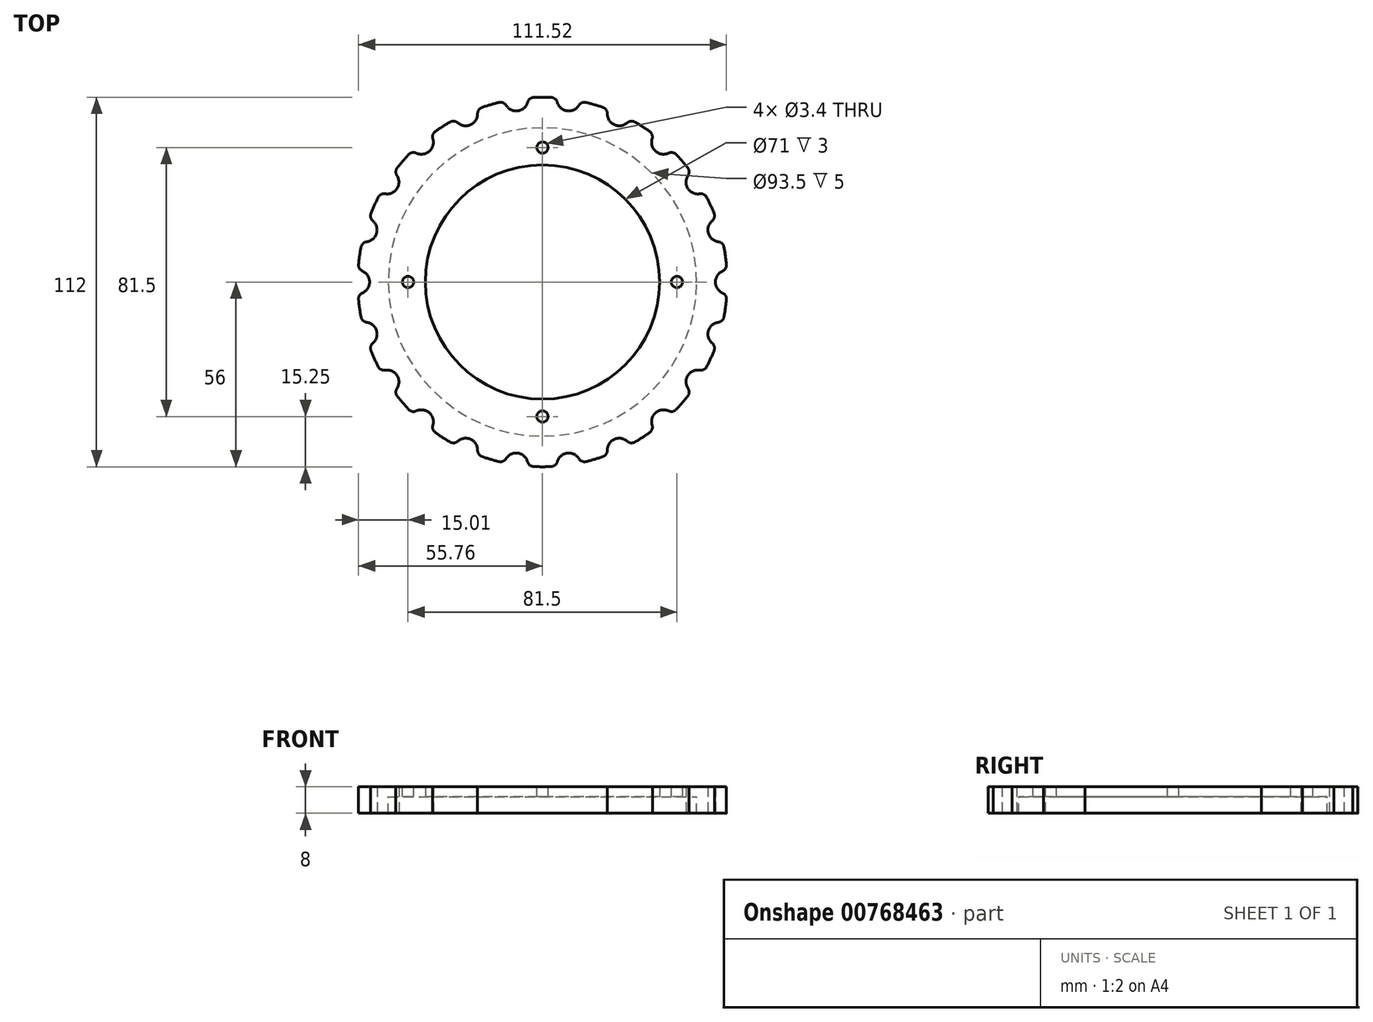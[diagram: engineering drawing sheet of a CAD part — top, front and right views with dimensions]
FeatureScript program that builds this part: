
annotation { "Feature Type Name" : "Feature", "Feature Type Description" : "" }
export const myFeature = defineFeature(function(context is Context, id is Id, definition is map)
    precondition{}
    {
        {
            var Q0;
            Q0=qCreatedBy(makeId("Top.planeOp"),FACE);
            var sketch = newSketch(context, id + "F0", { "sketchPlane" : qUnion([Q0])});
            skCircle(sketch, "E0", {"center": v(0, 0) * mm, "radius": 56 * mm});
            skCircle(sketch, "E1", {"center": v(56, 0) * mm, "radius": 3.6 * mm});
            skCircle(sketch, "E2.1.0", {"center": v(53.73, 15.78) * mm, "radius": 3.6 * mm});
            skCircle(sketch, "E2.2.0", {"center": v(47.11, 30.28) * mm, "radius": 3.6 * mm});
            skCircle(sketch, "E2.3.0", {"center": v(36.67, 42.32) * mm, "radius": 3.6 * mm});
            skCircle(sketch, "E2.4.0", {"center": v(23.26, 50.94) * mm, "radius": 3.6 * mm});
            skCircle(sketch, "E2.5.0", {"center": v(7.97, 55.43) * mm, "radius": 3.6 * mm});
            skCircle(sketch, "E2.6.0", {"center": v(-7.97, 55.43) * mm, "radius": 3.6 * mm});
            skCircle(sketch, "E2.7.0", {"center": v(-23.26, 50.94) * mm, "radius": 3.6 * mm});
            skCircle(sketch, "E2.8.0", {"center": v(-36.67, 42.32) * mm, "radius": 3.6 * mm});
            skCircle(sketch, "E2.9.0", {"center": v(-47.11, 30.28) * mm, "radius": 3.6 * mm});
            skCircle(sketch, "E2.10.0", {"center": v(-53.73, 15.78) * mm, "radius": 3.6 * mm});
            skCircle(sketch, "E2.11.0", {"center": v(-56, 0) * mm, "radius": 3.6 * mm});
            skCircle(sketch, "E2.12.0", {"center": v(-53.73, -15.78) * mm, "radius": 3.6 * mm});
            skCircle(sketch, "E2.13.0", {"center": v(-47.11, -30.28) * mm, "radius": 3.6 * mm});
            skCircle(sketch, "E2.14.0", {"center": v(-36.67, -42.32) * mm, "radius": 3.6 * mm});
            skCircle(sketch, "E2.15.0", {"center": v(-23.26, -50.94) * mm, "radius": 3.6 * mm});
            skCircle(sketch, "E2.16.0", {"center": v(-7.97, -55.43) * mm, "radius": 3.6 * mm});
            skCircle(sketch, "E2.17.0", {"center": v(7.97, -55.43) * mm, "radius": 3.6 * mm});
            skCircle(sketch, "E3.1.18.0", {"center": v(23.26, -50.94) * mm, "radius": 3.6 * mm});
            skCircle(sketch, "E4.1.19.0", {"center": v(36.67, -42.32) * mm, "radius": 3.6 * mm});
            skCircle(sketch, "E5.1.20.0", {"center": v(47.11, -30.28) * mm, "radius": 3.6 * mm});
            skCircle(sketch, "E6.1.21.0", {"center": v(53.73, -15.78) * mm, "radius": 3.6 * mm});
            skCircle(sketch, "E7", {"center": v(0, 0) * mm, "radius": 35.5 * mm});
            skSolve(sketch);
        }
        {
            var Q0;
            Q0=makeQuery(id+"F0.imprint","IMPRINT",FACE,{"disambiguationData":[TD([[makeQuery(id+"F0.imprint","IMPRINT",EDGE,{"derivedFrom":sQuery(id+"F0.wireOp",EDGE,"E0")}),1.0]])]});
            extrude(context, id + "F1", {"entities" : qUnion([Q0]), "depth" : 3 * mm, "offsetDistance" : 25 * mm});
        }
        {
            var Q0;
            {var subQ0=sQuery(id+"F0.wireOp",EDGE,"E2.7.0");var subQ1=sQuery(id+"F0.wireOp",EDGE,"E0");Q0=makeQuery(id+"F1.opExtrude","SWEPT_EDGE",EDGE,{"disambiguationData":[OSD([subQ1,subQ0]),TDD([makeQuery(id+"F0.imprint","INTERSECT",VERTEX,{"disambiguationData":[OD(1.0)],"derivedFrom":[subQ1,subQ0]})])]});}
            var Q1;
            {var subQ0=sQuery(id+"F0.wireOp",EDGE,"E2.8.0");var subQ1=sQuery(id+"F0.wireOp",EDGE,"E0");Q1=makeQuery(id+"F1.opExtrude","SWEPT_EDGE",EDGE,{"disambiguationData":[OSD([subQ1,subQ0]),TDD([makeQuery(id+"F0.imprint","INTERSECT",VERTEX,{"disambiguationData":[OD(0.0)],"derivedFrom":[subQ1,subQ0]})])]});}
            var Q2;
            {var subQ0=sQuery(id+"F0.wireOp",EDGE,"E2.8.0");var subQ1=sQuery(id+"F0.wireOp",EDGE,"E0");Q2=makeQuery(id+"F1.opExtrude","SWEPT_EDGE",EDGE,{"disambiguationData":[OSD([subQ1,subQ0]),TDD([makeQuery(id+"F0.imprint","INTERSECT",VERTEX,{"disambiguationData":[OD(1.0)],"derivedFrom":[subQ1,subQ0]})])]});}
            var Q3;
            {var subQ0=sQuery(id+"F0.wireOp",EDGE,"E2.9.0");var subQ1=sQuery(id+"F0.wireOp",EDGE,"E0");Q3=makeQuery(id+"F1.opExtrude","SWEPT_EDGE",EDGE,{"disambiguationData":[OSD([subQ1,subQ0]),TDD([makeQuery(id+"F0.imprint","INTERSECT",VERTEX,{"disambiguationData":[OD(0.0)],"derivedFrom":[subQ1,subQ0]})])]});}
            var Q4;
            {var subQ0=sQuery(id+"F0.wireOp",EDGE,"E2.9.0");var subQ1=sQuery(id+"F0.wireOp",EDGE,"E0");Q4=makeQuery(id+"F1.opExtrude","SWEPT_EDGE",EDGE,{"disambiguationData":[OSD([subQ1,subQ0]),TDD([makeQuery(id+"F0.imprint","INTERSECT",VERTEX,{"disambiguationData":[OD(1.0)],"derivedFrom":[subQ1,subQ0]})])]});}
            var Q5;
            {var subQ0=sQuery(id+"F0.wireOp",EDGE,"E2.10.0");var subQ1=sQuery(id+"F0.wireOp",EDGE,"E0");Q5=makeQuery(id+"F1.opExtrude","SWEPT_EDGE",EDGE,{"disambiguationData":[OSD([subQ1,subQ0]),TDD([makeQuery(id+"F0.imprint","INTERSECT",VERTEX,{"disambiguationData":[OD(0.0)],"derivedFrom":[subQ1,subQ0]})])]});}
            var Q6;
            {var subQ0=sQuery(id+"F0.wireOp",EDGE,"E2.10.0");var subQ1=sQuery(id+"F0.wireOp",EDGE,"E0");Q6=makeQuery(id+"F1.opExtrude","SWEPT_EDGE",EDGE,{"disambiguationData":[OSD([subQ1,subQ0]),TDD([makeQuery(id+"F0.imprint","INTERSECT",VERTEX,{"disambiguationData":[OD(1.0)],"derivedFrom":[subQ1,subQ0]})])]});}
            var Q7;
            {var subQ0=sQuery(id+"F0.wireOp",EDGE,"E2.11.0");var subQ1=sQuery(id+"F0.wireOp",EDGE,"E0");Q7=makeQuery(id+"F1.opExtrude","SWEPT_EDGE",EDGE,{"disambiguationData":[OSD([subQ1,subQ0]),TDD([makeQuery(id+"F0.imprint","INTERSECT",VERTEX,{"disambiguationData":[OD(0.0)],"derivedFrom":[subQ1,subQ0]})])]});}
            var Q8;
            {var subQ0=sQuery(id+"F0.wireOp",EDGE,"E2.11.0");var subQ1=sQuery(id+"F0.wireOp",EDGE,"E0");Q8=makeQuery(id+"F1.opExtrude","SWEPT_EDGE",EDGE,{"disambiguationData":[OSD([subQ1,subQ0]),TDD([makeQuery(id+"F0.imprint","INTERSECT",VERTEX,{"disambiguationData":[OD(1.0)],"derivedFrom":[subQ1,subQ0]})])]});}
            var Q9;
            {var subQ0=sQuery(id+"F0.wireOp",EDGE,"E2.12.0");var subQ1=sQuery(id+"F0.wireOp",EDGE,"E0");Q9=makeQuery(id+"F1.opExtrude","SWEPT_EDGE",EDGE,{"disambiguationData":[OSD([subQ1,subQ0]),TDD([makeQuery(id+"F0.imprint","INTERSECT",VERTEX,{"disambiguationData":[OD(0.0)],"derivedFrom":[subQ1,subQ0]})])]});}
            var Q10;
            {var subQ0=sQuery(id+"F0.wireOp",EDGE,"E2.12.0");var subQ1=sQuery(id+"F0.wireOp",EDGE,"E0");Q10=makeQuery(id+"F1.opExtrude","SWEPT_EDGE",EDGE,{"disambiguationData":[OSD([subQ1,subQ0]),TDD([makeQuery(id+"F0.imprint","INTERSECT",VERTEX,{"disambiguationData":[OD(1.0)],"derivedFrom":[subQ1,subQ0]})])]});}
            var Q11;
            {var subQ0=sQuery(id+"F0.wireOp",EDGE,"E2.13.0");var subQ1=sQuery(id+"F0.wireOp",EDGE,"E0");Q11=makeQuery(id+"F1.opExtrude","SWEPT_EDGE",EDGE,{"disambiguationData":[OSD([subQ1,subQ0]),TDD([makeQuery(id+"F0.imprint","INTERSECT",VERTEX,{"disambiguationData":[OD(0.0)],"derivedFrom":[subQ1,subQ0]})])]});}
            var Q12;
            {var subQ0=sQuery(id+"F0.wireOp",EDGE,"E2.13.0");var subQ1=sQuery(id+"F0.wireOp",EDGE,"E0");Q12=makeQuery(id+"F1.opExtrude","SWEPT_EDGE",EDGE,{"disambiguationData":[OSD([subQ1,subQ0]),TDD([makeQuery(id+"F0.imprint","INTERSECT",VERTEX,{"disambiguationData":[OD(1.0)],"derivedFrom":[subQ1,subQ0]})])]});}
            var Q13;
            {var subQ0=sQuery(id+"F0.wireOp",EDGE,"E2.14.0");var subQ1=sQuery(id+"F0.wireOp",EDGE,"E0");Q13=makeQuery(id+"F1.opExtrude","SWEPT_EDGE",EDGE,{"disambiguationData":[OSD([subQ1,subQ0]),TDD([makeQuery(id+"F0.imprint","INTERSECT",VERTEX,{"disambiguationData":[OD(0.0)],"derivedFrom":[subQ1,subQ0]})])]});}
            var Q14;
            {var subQ0=sQuery(id+"F0.wireOp",EDGE,"E2.14.0");var subQ1=sQuery(id+"F0.wireOp",EDGE,"E0");Q14=makeQuery(id+"F1.opExtrude","SWEPT_EDGE",EDGE,{"disambiguationData":[OSD([subQ1,subQ0]),TDD([makeQuery(id+"F0.imprint","INTERSECT",VERTEX,{"disambiguationData":[OD(1.0)],"derivedFrom":[subQ1,subQ0]})])]});}
            var Q15;
            {var subQ0=sQuery(id+"F0.wireOp",EDGE,"E2.15.0");var subQ1=sQuery(id+"F0.wireOp",EDGE,"E0");Q15=makeQuery(id+"F1.opExtrude","SWEPT_EDGE",EDGE,{"disambiguationData":[OSD([subQ1,subQ0]),TDD([makeQuery(id+"F0.imprint","INTERSECT",VERTEX,{"disambiguationData":[OD(0.0)],"derivedFrom":[subQ1,subQ0]})])]});}
            var Q16;
            {var subQ0=sQuery(id+"F0.wireOp",EDGE,"E2.15.0");var subQ1=sQuery(id+"F0.wireOp",EDGE,"E0");Q16=makeQuery(id+"F1.opExtrude","SWEPT_EDGE",EDGE,{"disambiguationData":[OSD([subQ1,subQ0]),TDD([makeQuery(id+"F0.imprint","INTERSECT",VERTEX,{"disambiguationData":[OD(1.0)],"derivedFrom":[subQ1,subQ0]})])]});}
            var Q17;
            {var subQ0=sQuery(id+"F0.wireOp",EDGE,"E2.16.0");var subQ1=sQuery(id+"F0.wireOp",EDGE,"E0");Q17=makeQuery(id+"F1.opExtrude","SWEPT_EDGE",EDGE,{"disambiguationData":[OSD([subQ1,subQ0]),TDD([makeQuery(id+"F0.imprint","INTERSECT",VERTEX,{"disambiguationData":[OD(0.0)],"derivedFrom":[subQ1,subQ0]})])]});}
            var Q18;
            {var subQ0=sQuery(id+"F0.wireOp",EDGE,"E2.16.0");var subQ1=sQuery(id+"F0.wireOp",EDGE,"E0");Q18=makeQuery(id+"F1.opExtrude","SWEPT_EDGE",EDGE,{"disambiguationData":[OSD([subQ1,subQ0]),TDD([makeQuery(id+"F0.imprint","INTERSECT",VERTEX,{"disambiguationData":[OD(1.0)],"derivedFrom":[subQ1,subQ0]})])]});}
            var Q19;
            {var subQ0=sQuery(id+"F0.wireOp",EDGE,"E2.17.0");var subQ1=sQuery(id+"F0.wireOp",EDGE,"E0");Q19=makeQuery(id+"F1.opExtrude","SWEPT_EDGE",EDGE,{"disambiguationData":[OSD([subQ1,subQ0]),TDD([makeQuery(id+"F0.imprint","INTERSECT",VERTEX,{"disambiguationData":[OD(0.0)],"derivedFrom":[subQ1,subQ0]})])]});}
            var Q20;
            {var subQ0=sQuery(id+"F0.wireOp",EDGE,"E2.17.0");var subQ1=sQuery(id+"F0.wireOp",EDGE,"E0");Q20=makeQuery(id+"F1.opExtrude","SWEPT_EDGE",EDGE,{"disambiguationData":[OSD([subQ1,subQ0]),TDD([makeQuery(id+"F0.imprint","INTERSECT",VERTEX,{"disambiguationData":[OD(1.0)],"derivedFrom":[subQ1,subQ0]})])]});}
            var Q21;
            {var subQ0=sQuery(id+"F0.wireOp",EDGE,"E3.1.18.0");var subQ1=sQuery(id+"F0.wireOp",EDGE,"E0");Q21=makeQuery(id+"F1.opExtrude","SWEPT_EDGE",EDGE,{"disambiguationData":[OSD([subQ1,subQ0]),TDD([makeQuery(id+"F0.imprint","INTERSECT",VERTEX,{"disambiguationData":[OD(0.0)],"derivedFrom":[subQ1,subQ0]})])]});}
            var Q22;
            {var subQ0=sQuery(id+"F0.wireOp",EDGE,"E4.1.19.0");var subQ1=sQuery(id+"F0.wireOp",EDGE,"E0");Q22=makeQuery(id+"F1.opExtrude","SWEPT_EDGE",EDGE,{"disambiguationData":[OSD([subQ1,subQ0]),TDD([makeQuery(id+"F0.imprint","INTERSECT",VERTEX,{"disambiguationData":[OD(0.0)],"derivedFrom":[subQ1,subQ0]})])]});}
            var Q23;
            {var subQ0=sQuery(id+"F0.wireOp",EDGE,"E3.1.18.0");var subQ1=sQuery(id+"F0.wireOp",EDGE,"E0");Q23=makeQuery(id+"F1.opExtrude","SWEPT_EDGE",EDGE,{"disambiguationData":[OSD([subQ1,subQ0]),TDD([makeQuery(id+"F0.imprint","INTERSECT",VERTEX,{"disambiguationData":[OD(1.0)],"derivedFrom":[subQ1,subQ0]})])]});}
            var Q24;
            {var subQ0=sQuery(id+"F0.wireOp",EDGE,"E4.1.19.0");var subQ1=sQuery(id+"F0.wireOp",EDGE,"E0");Q24=makeQuery(id+"F1.opExtrude","SWEPT_EDGE",EDGE,{"disambiguationData":[OSD([subQ1,subQ0]),TDD([makeQuery(id+"F0.imprint","INTERSECT",VERTEX,{"disambiguationData":[OD(1.0)],"derivedFrom":[subQ1,subQ0]})])]});}
            var Q25;
            {var subQ0=sQuery(id+"F0.wireOp",EDGE,"E5.1.20.0");var subQ1=sQuery(id+"F0.wireOp",EDGE,"E0");Q25=makeQuery(id+"F1.opExtrude","SWEPT_EDGE",EDGE,{"disambiguationData":[OSD([subQ1,subQ0]),TDD([makeQuery(id+"F0.imprint","INTERSECT",VERTEX,{"disambiguationData":[OD(0.0)],"derivedFrom":[subQ1,subQ0]})])]});}
            var Q26;
            {var subQ0=sQuery(id+"F0.wireOp",EDGE,"E6.1.21.0");var subQ1=sQuery(id+"F0.wireOp",EDGE,"E0");Q26=makeQuery(id+"F1.opExtrude","SWEPT_EDGE",EDGE,{"disambiguationData":[OSD([subQ1,subQ0]),TDD([makeQuery(id+"F0.imprint","INTERSECT",VERTEX,{"disambiguationData":[OD(0.0)],"derivedFrom":[subQ1,subQ0]})])]});}
            var Q27;
            {var subQ0=sQuery(id+"F0.wireOp",EDGE,"E5.1.20.0");var subQ1=sQuery(id+"F0.wireOp",EDGE,"E0");Q27=makeQuery(id+"F1.opExtrude","SWEPT_EDGE",EDGE,{"disambiguationData":[OSD([subQ1,subQ0]),TDD([makeQuery(id+"F0.imprint","INTERSECT",VERTEX,{"disambiguationData":[OD(1.0)],"derivedFrom":[subQ1,subQ0]})])]});}
            var Q28;
            {var subQ0=sQuery(id+"F0.wireOp",EDGE,"E1");var subQ1=sQuery(id+"F0.wireOp",EDGE,"E0");Q28=makeQuery(id+"F1.opExtrude","SWEPT_EDGE",EDGE,{"disambiguationData":[OSD([subQ1,subQ0]),TDD([makeQuery(id+"F0.imprint","INTERSECT",VERTEX,{"disambiguationData":[OD(1.0)],"derivedFrom":[subQ1,subQ0]})])]});}
            var Q29;
            {var subQ0=sQuery(id+"F0.wireOp",EDGE,"E6.1.21.0");var subQ1=sQuery(id+"F0.wireOp",EDGE,"E0");Q29=makeQuery(id+"F1.opExtrude","SWEPT_EDGE",EDGE,{"disambiguationData":[OSD([subQ1,subQ0]),TDD([makeQuery(id+"F0.imprint","INTERSECT",VERTEX,{"disambiguationData":[OD(1.0)],"derivedFrom":[subQ1,subQ0]})])]});}
            var Q30;
            {var subQ0=sQuery(id+"F0.wireOp",EDGE,"E1");var subQ1=sQuery(id+"F0.wireOp",EDGE,"E0");Q30=makeQuery(id+"F1.opExtrude","SWEPT_EDGE",EDGE,{"disambiguationData":[OSD([subQ1,subQ0]),TDD([makeQuery(id+"F0.imprint","INTERSECT",VERTEX,{"disambiguationData":[OD(0.0)],"derivedFrom":[subQ1,subQ0]})])]});}
            var Q31;
            {var subQ0=sQuery(id+"F0.wireOp",EDGE,"E2.1.0");var subQ1=sQuery(id+"F0.wireOp",EDGE,"E0");Q31=makeQuery(id+"F1.opExtrude","SWEPT_EDGE",EDGE,{"disambiguationData":[OSD([subQ1,subQ0]),TDD([makeQuery(id+"F0.imprint","INTERSECT",VERTEX,{"disambiguationData":[OD(0.0)],"derivedFrom":[subQ1,subQ0]})])]});}
            var Q32;
            {var subQ0=sQuery(id+"F0.wireOp",EDGE,"E2.1.0");var subQ1=sQuery(id+"F0.wireOp",EDGE,"E0");Q32=makeQuery(id+"F1.opExtrude","SWEPT_EDGE",EDGE,{"disambiguationData":[OSD([subQ1,subQ0]),TDD([makeQuery(id+"F0.imprint","INTERSECT",VERTEX,{"disambiguationData":[OD(1.0)],"derivedFrom":[subQ1,subQ0]})])]});}
            var Q33;
            {var subQ0=sQuery(id+"F0.wireOp",EDGE,"E2.2.0");var subQ1=sQuery(id+"F0.wireOp",EDGE,"E0");Q33=makeQuery(id+"F1.opExtrude","SWEPT_EDGE",EDGE,{"disambiguationData":[OSD([subQ1,subQ0]),TDD([makeQuery(id+"F0.imprint","INTERSECT",VERTEX,{"disambiguationData":[OD(0.0)],"derivedFrom":[subQ1,subQ0]})])]});}
            var Q34;
            {var subQ0=sQuery(id+"F0.wireOp",EDGE,"E2.2.0");var subQ1=sQuery(id+"F0.wireOp",EDGE,"E0");Q34=makeQuery(id+"F1.opExtrude","SWEPT_EDGE",EDGE,{"disambiguationData":[OSD([subQ1,subQ0]),TDD([makeQuery(id+"F0.imprint","INTERSECT",VERTEX,{"disambiguationData":[OD(1.0)],"derivedFrom":[subQ1,subQ0]})])]});}
            var Q35;
            {var subQ0=sQuery(id+"F0.wireOp",EDGE,"E2.3.0");var subQ1=sQuery(id+"F0.wireOp",EDGE,"E0");Q35=makeQuery(id+"F1.opExtrude","SWEPT_EDGE",EDGE,{"disambiguationData":[OSD([subQ1,subQ0]),TDD([makeQuery(id+"F0.imprint","INTERSECT",VERTEX,{"disambiguationData":[OD(0.0)],"derivedFrom":[subQ1,subQ0]})])]});}
            var Q36;
            {var subQ0=sQuery(id+"F0.wireOp",EDGE,"E2.3.0");var subQ1=sQuery(id+"F0.wireOp",EDGE,"E0");Q36=makeQuery(id+"F1.opExtrude","SWEPT_EDGE",EDGE,{"disambiguationData":[OSD([subQ1,subQ0]),TDD([makeQuery(id+"F0.imprint","INTERSECT",VERTEX,{"disambiguationData":[OD(1.0)],"derivedFrom":[subQ1,subQ0]})])]});}
            var Q37;
            {var subQ0=sQuery(id+"F0.wireOp",EDGE,"E2.4.0");var subQ1=sQuery(id+"F0.wireOp",EDGE,"E0");Q37=makeQuery(id+"F1.opExtrude","SWEPT_EDGE",EDGE,{"disambiguationData":[OSD([subQ1,subQ0]),TDD([makeQuery(id+"F0.imprint","INTERSECT",VERTEX,{"disambiguationData":[OD(0.0)],"derivedFrom":[subQ1,subQ0]})])]});}
            var Q38;
            {var subQ0=sQuery(id+"F0.wireOp",EDGE,"E2.4.0");var subQ1=sQuery(id+"F0.wireOp",EDGE,"E0");Q38=makeQuery(id+"F1.opExtrude","SWEPT_EDGE",EDGE,{"disambiguationData":[OSD([subQ1,subQ0]),TDD([makeQuery(id+"F0.imprint","INTERSECT",VERTEX,{"disambiguationData":[OD(1.0)],"derivedFrom":[subQ1,subQ0]})])]});}
            var Q39;
            {var subQ0=sQuery(id+"F0.wireOp",EDGE,"E2.5.0");var subQ1=sQuery(id+"F0.wireOp",EDGE,"E0");Q39=makeQuery(id+"F1.opExtrude","SWEPT_EDGE",EDGE,{"disambiguationData":[OSD([subQ1,subQ0]),TDD([makeQuery(id+"F0.imprint","INTERSECT",VERTEX,{"disambiguationData":[OD(0.0)],"derivedFrom":[subQ1,subQ0]})])]});}
            var Q40;
            {var subQ0=sQuery(id+"F0.wireOp",EDGE,"E2.5.0");var subQ1=sQuery(id+"F0.wireOp",EDGE,"E0");Q40=makeQuery(id+"F1.opExtrude","SWEPT_EDGE",EDGE,{"disambiguationData":[OSD([subQ1,subQ0]),TDD([makeQuery(id+"F0.imprint","INTERSECT",VERTEX,{"disambiguationData":[OD(1.0)],"derivedFrom":[subQ1,subQ0]})])]});}
            var Q41;
            {var subQ0=sQuery(id+"F0.wireOp",EDGE,"E2.6.0");var subQ1=sQuery(id+"F0.wireOp",EDGE,"E0");Q41=makeQuery(id+"F1.opExtrude","SWEPT_EDGE",EDGE,{"disambiguationData":[OSD([subQ1,subQ0]),TDD([makeQuery(id+"F0.imprint","INTERSECT",VERTEX,{"disambiguationData":[OD(0.0)],"derivedFrom":[subQ1,subQ0]})])]});}
            var Q42;
            {var subQ0=sQuery(id+"F0.wireOp",EDGE,"E2.7.0");var subQ1=sQuery(id+"F0.wireOp",EDGE,"E0");Q42=makeQuery(id+"F1.opExtrude","SWEPT_EDGE",EDGE,{"disambiguationData":[OSD([subQ1,subQ0]),TDD([makeQuery(id+"F0.imprint","INTERSECT",VERTEX,{"disambiguationData":[OD(0.0)],"derivedFrom":[subQ1,subQ0]})])]});}
            var Q43;
            {var subQ0=sQuery(id+"F0.wireOp",EDGE,"E2.6.0");var subQ1=sQuery(id+"F0.wireOp",EDGE,"E0");Q43=makeQuery(id+"F1.opExtrude","SWEPT_EDGE",EDGE,{"disambiguationData":[OSD([subQ1,subQ0]),TDD([makeQuery(id+"F0.imprint","INTERSECT",VERTEX,{"disambiguationData":[OD(1.0)],"derivedFrom":[subQ1,subQ0]})])]});}
            fillet(context, id + "F2", {"entities" : qUnion([Q0, Q1, Q2, Q3, Q4, Q5, Q6, Q7, Q8, Q9, Q10, Q11, Q12, Q13, Q14, Q15, Q16, Q17, Q18, Q19, Q20, Q21, Q22, Q23, Q24, Q25, Q26, Q27, Q28, Q29, Q30, Q31, Q32, Q33, Q34, Q35, Q36, Q37, Q38, Q39, Q40, Q41, Q42, Q43]), "tangentPropagation" : true, "radius" : 2 * mm, "defaultsChanged" : false, "vertexSettings" : [], "allowEdgeOverflow" : false});
        }
        {
            var Q0;
            Q0=makeQuery(id+"F1.opExtrude","CAP_FACE",FACE,{"disambiguationData":[OSD([sQuery(id+"F0.wireOp",EDGE,"E0"),sQuery(id+"F0.wireOp",EDGE,"E1"),sQuery(id+"F0.wireOp",EDGE,"E2.1.0"),sQuery(id+"F0.wireOp",EDGE,"E2.2.0"),sQuery(id+"F0.wireOp",EDGE,"E2.3.0"),sQuery(id+"F0.wireOp",EDGE,"E2.4.0"),sQuery(id+"F0.wireOp",EDGE,"E2.5.0"),sQuery(id+"F0.wireOp",EDGE,"E2.6.0"),sQuery(id+"F0.wireOp",EDGE,"E2.7.0"),sQuery(id+"F0.wireOp",EDGE,"E2.8.0"),sQuery(id+"F0.wireOp",EDGE,"E2.9.0"),sQuery(id+"F0.wireOp",EDGE,"E2.10.0"),sQuery(id+"F0.wireOp",EDGE,"E2.11.0"),sQuery(id+"F0.wireOp",EDGE,"E2.12.0"),sQuery(id+"F0.wireOp",EDGE,"E2.13.0"),sQuery(id+"F0.wireOp",EDGE,"E2.14.0"),sQuery(id+"F0.wireOp",EDGE,"E2.15.0"),sQuery(id+"F0.wireOp",EDGE,"E2.16.0"),sQuery(id+"F0.wireOp",EDGE,"E2.17.0"),sQuery(id+"F0.wireOp",EDGE,"E3.1.18.0"),sQuery(id+"F0.wireOp",EDGE,"E4.1.19.0"),sQuery(id+"F0.wireOp",EDGE,"E5.1.20.0"),sQuery(id+"F0.wireOp",EDGE,"E6.1.21.0"),sQuery(id+"F0.wireOp",EDGE,"E7")])],"isStart":false});
            var sketch = newSketch(context, id + "F3", { "sketchPlane" : qUnion([Q0])});
            skLineSegment(sketch, "E8", {"start": v(-40.75, 0) * mm, "end": v(0, 40.75) * mm});
            skLineSegment(sketch, "E9", {"start": v(0, 40.75) * mm, "end": v(40.75, 0) * mm});
            skLineSegment(sketch, "E10", {"start": v(40.75, 0) * mm, "end": v(0, -40.75) * mm});
            skLineSegment(sketch, "E11", {"start": v(0, -40.75) * mm, "end": v(-40.75, 0) * mm});
            skSolve(sketch);
        }
        {
            var Q0;
            Q0=sQuery(id+"F3.wireOp",VERTEX,"E8.end");
            var Q1;
            Q1=sQuery(id+"F3.wireOp",VERTEX,"E9.end");
            var Q2;
            Q2=sQuery(id+"F3.wireOp",VERTEX,"E10.end");
            var Q3;
            Q3=sQuery(id+"F3.wireOp",VERTEX,"E8.start");
            var Q4;
            Q4=makeQuery(id+"F1.opExtrude","SWEPT_BODY",BODY,{"disambiguationData":[OSD([sQuery(id+"F0.wireOp",EDGE,"E0"),sQuery(id+"F0.wireOp",EDGE,"E1"),sQuery(id+"F0.wireOp",EDGE,"E2.1.0"),sQuery(id+"F0.wireOp",EDGE,"E2.2.0"),sQuery(id+"F0.wireOp",EDGE,"E2.3.0"),sQuery(id+"F0.wireOp",EDGE,"E2.4.0"),sQuery(id+"F0.wireOp",EDGE,"E2.5.0"),sQuery(id+"F0.wireOp",EDGE,"E2.6.0"),sQuery(id+"F0.wireOp",EDGE,"E2.7.0"),sQuery(id+"F0.wireOp",EDGE,"E2.8.0"),sQuery(id+"F0.wireOp",EDGE,"E2.9.0"),sQuery(id+"F0.wireOp",EDGE,"E2.10.0"),sQuery(id+"F0.wireOp",EDGE,"E2.11.0"),sQuery(id+"F0.wireOp",EDGE,"E2.12.0"),sQuery(id+"F0.wireOp",EDGE,"E2.13.0"),sQuery(id+"F0.wireOp",EDGE,"E2.14.0"),sQuery(id+"F0.wireOp",EDGE,"E2.15.0"),sQuery(id+"F0.wireOp",EDGE,"E2.16.0"),sQuery(id+"F0.wireOp",EDGE,"E2.17.0"),sQuery(id+"F0.wireOp",EDGE,"E3.1.18.0"),sQuery(id+"F0.wireOp",EDGE,"E4.1.19.0"),sQuery(id+"F0.wireOp",EDGE,"E5.1.20.0"),sQuery(id+"F0.wireOp",EDGE,"E6.1.21.0"),sQuery(id+"F0.wireOp",EDGE,"E7")])]});
            hole(context, id + "F4", {"style" : HoleStyle.SIMPLE, "endStyle" : HoleEndStyle.THROUGH, "standardTappedOrClearance" : lookupTablePath({ "fit" : "Normal", "standard" : "ISO", "size" : "M3", "type" : "Clearance" }), "standardBlindInLast" : lookupTablePath({ "fit" : "Normal", "standard" : "ISO", "engagement" : "75%", "pitch" : "0.5 mm", "size" : "M3", "type" : "Clearance & tapped" }), "holeDiameter" : 3.4 * mm, "majorDiameter" : 5 * mm, "isTappedThrough" : true, "tappedDepth" : 12 * mm, "tapClearance" : 3, "locations" : qUnion([Q0, Q1, Q2, Q3]), "scope" : qUnion([Q4])});
        }
        {
            var Q0;
            Q0=makeQuery(id+"F1.opExtrude","CAP_FACE",FACE,{"disambiguationData":[OSD([sQuery(id+"F0.wireOp",EDGE,"E0"),sQuery(id+"F0.wireOp",EDGE,"E1"),sQuery(id+"F0.wireOp",EDGE,"E2.1.0"),sQuery(id+"F0.wireOp",EDGE,"E2.2.0"),sQuery(id+"F0.wireOp",EDGE,"E2.3.0"),sQuery(id+"F0.wireOp",EDGE,"E2.4.0"),sQuery(id+"F0.wireOp",EDGE,"E2.5.0"),sQuery(id+"F0.wireOp",EDGE,"E2.6.0"),sQuery(id+"F0.wireOp",EDGE,"E2.7.0"),sQuery(id+"F0.wireOp",EDGE,"E2.8.0"),sQuery(id+"F0.wireOp",EDGE,"E2.9.0"),sQuery(id+"F0.wireOp",EDGE,"E2.10.0"),sQuery(id+"F0.wireOp",EDGE,"E2.11.0"),sQuery(id+"F0.wireOp",EDGE,"E2.12.0"),sQuery(id+"F0.wireOp",EDGE,"E2.13.0"),sQuery(id+"F0.wireOp",EDGE,"E2.14.0"),sQuery(id+"F0.wireOp",EDGE,"E2.15.0"),sQuery(id+"F0.wireOp",EDGE,"E2.16.0"),sQuery(id+"F0.wireOp",EDGE,"E2.17.0"),sQuery(id+"F0.wireOp",EDGE,"E3.1.18.0"),sQuery(id+"F0.wireOp",EDGE,"E4.1.19.0"),sQuery(id+"F0.wireOp",EDGE,"E5.1.20.0"),sQuery(id+"F0.wireOp",EDGE,"E6.1.21.0"),sQuery(id+"F0.wireOp",EDGE,"E7")])],"isStart":true});
            var sketch = newSketch(context, id + "F5", { "sketchPlane" : qUnion([Q0])});
            skCircle(sketch, "E12", {"center": v(0, 0) * mm, "radius": 46.75 * mm});
            skSolve(sketch);
        }
        {
            var Q0;
            Q0=makeQuery(id+"F5.imprint","IMPRINT",FACE,{"disambiguationData":[TD([[makeQuery(id+"F5.imprint","IMPRINT",EDGE,{"derivedFrom":sQuery(id+"F5.wireOp",EDGE,"E12")}),-1.0]])]});
            extrude(context, id + "F6", {"entities" : qUnion([Q0]), "operationType" : NewBodyOperationType.ADD, "depth" : 5 * mm, "offsetDistance" : 25 * mm});
        }
    });
